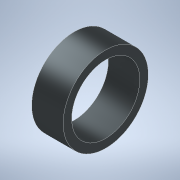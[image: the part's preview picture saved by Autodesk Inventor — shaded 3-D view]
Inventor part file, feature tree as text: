
AUTODESK INVENTOR PART (.ipt)
format: ipt  version: 2021 (Build 250183000, 183)  size: 108,032 bytes
history: native  units: mm
features: extrude x1, sketch x1
ambient origin geometry x8: Origin, YZ Plane, XZ Plane, XY Plane, X Axis, Y Axis, Z Axis, Center Point
bodies: Solid1 (feature_tree)
feature tree (2):
  extrude  "Extrusion1"  Depth=18.5mm
  sketch  "Sketch1"  dims[d0=40.0mm d1=50.0mm d2=18.5mm d3=0.0mm]
